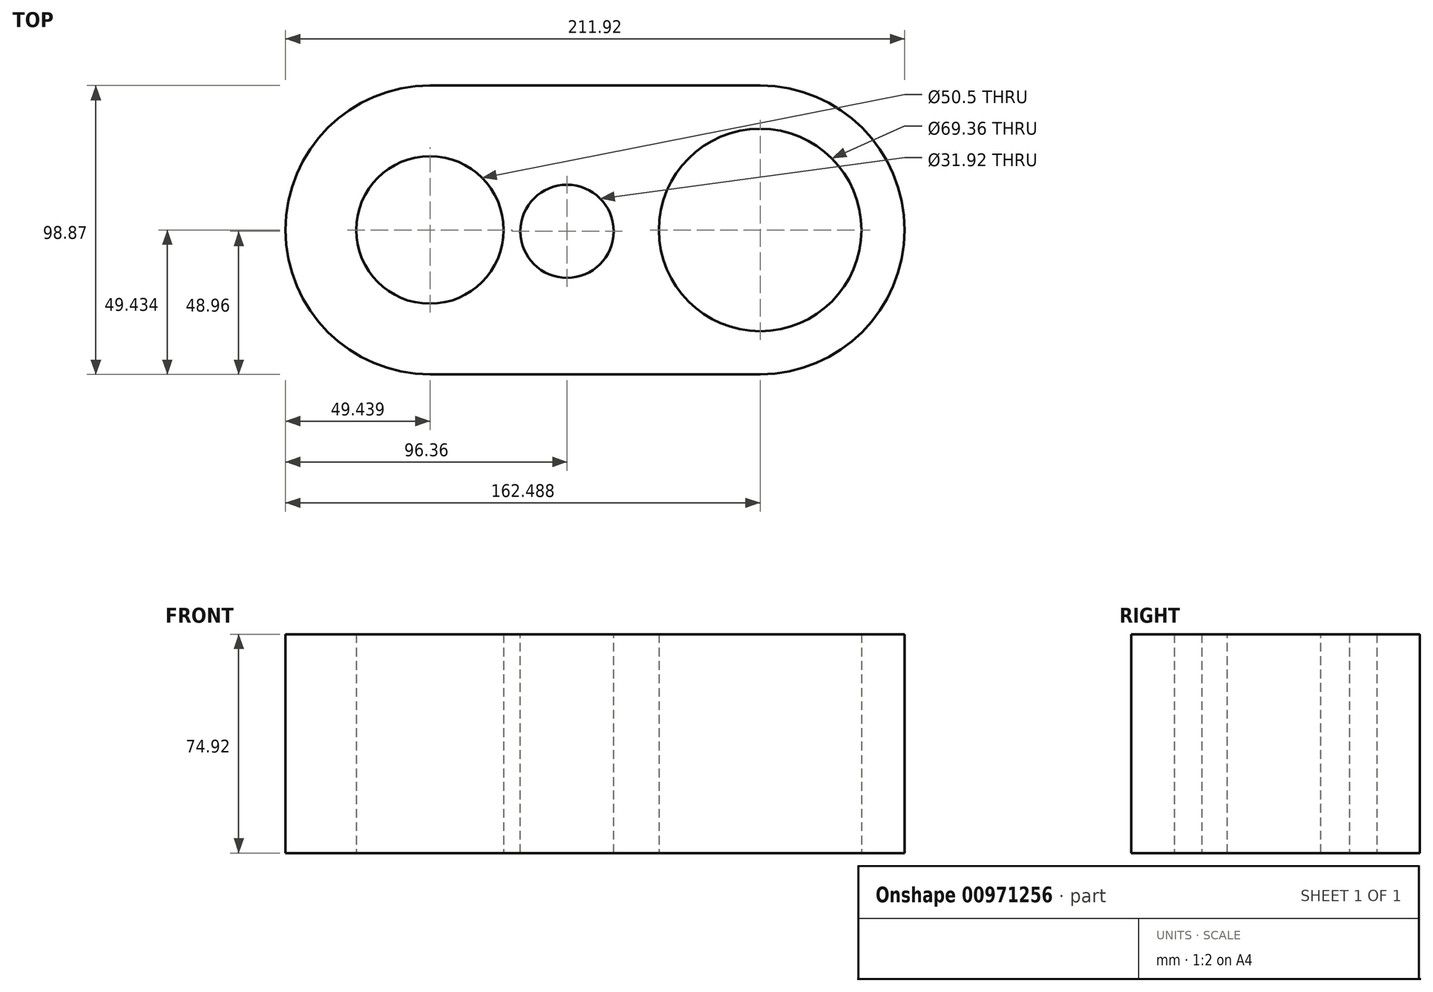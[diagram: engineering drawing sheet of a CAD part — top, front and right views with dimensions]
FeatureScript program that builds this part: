
annotation { "Feature Type Name" : "Feature", "Feature Type Description" : "" }
export const myFeature = defineFeature(function(context is Context, id is Id, definition is map)
    precondition{}
    {
        {
            var Q0;
            Q0=qCreatedBy(makeId("Top.planeOp"),FACE);
            var sketch = newSketch(context, id + "F0", { "sketchPlane" : qUnion([Q0])});
            skLineSegment(sketch, "E0", {"start": v(-46.92, 37.12) * mm, "end": v(66.13, 37.12) * mm});
            skLineSegment(sketch, "E1", {"start": v(-46.92, -61.75) * mm, "end": v(66.13, -61.75) * mm});
            skArc(sketch, "E2", {"start": v(-46.92, 37.12) * mm, "mid": v(-96.36, -12.32) * mm, "end": v(-46.92, -61.75) * mm});
            skArc(sketch, "E3", {"start": v(66.13, -61.75) * mm, "mid": v(115.56, -12.32) * mm, "end": v(66.13, 37.12) * mm});
            skCircle(sketch, "E4", {"center": v(-46.92, -12.32) * mm, "radius": 25.25 * mm});
            skCircle(sketch, "E5", {"center": v(66.13, -12.32) * mm, "radius": 34.68 * mm});
            skSolve(sketch);
        }
        {
            var Q0;
            Q0=makeQuery(id+"F0.imprint","IMPRINT",FACE,{"disambiguationData":[TD([[makeQuery(id+"F0.imprint","IMPRINT",EDGE,{"derivedFrom":sQuery(id+"F0.wireOp",EDGE,"E0")}),-1.0]])]});
            extrude(context, id + "F1", {"entities" : qUnion([Q0]), "depth" : 74.92 * mm, "offsetDistance" : 25.4 * mm});
        }
        {
            var Q0;
            Q0=makeQuery(id+"F1.opExtrude","CAP_FACE",FACE,{"disambiguationData":[OSD([sQuery(id+"F0.wireOp",EDGE,"E0"),sQuery(id+"F0.wireOp",EDGE,"E1"),sQuery(id+"F0.wireOp",EDGE,"E2"),sQuery(id+"F0.wireOp",EDGE,"E3"),sQuery(id+"F0.wireOp",EDGE,"E4"),sQuery(id+"F0.wireOp",EDGE,"E5")])],"isStart":false});
            var sketch = newSketch(context, id + "F2", { "sketchPlane" : qUnion([Q0])});
            skLineSegment(sketch, "E6", {"start": v(-46.92, -12.32) * mm, "end": v(66.13, -12.32) * mm, "construction": true});
            skSolve(sketch);
        }
        {
            var Q0;
            Q0=makeQuery(id+"F2.imprint","IMPRINT",FACE,{"disambiguationData":[TD([[makeQuery(id+"F2.imprint","IMPRINT",EDGE,{"derivedFrom":makeQuery(id+"F1.opExtrude","CAP_EDGE",EDGE,{"disambiguationData":[OSD([sQuery(id+"F0.wireOp",EDGE,"E0")])],"isStart":false})}),-1.0]])]});
            var sketch = newSketch(context, id + "F3", { "sketchPlane" : qUnion([Q0])});
            skCircle(sketch, "E7", {"center": v(0, -12.8) * mm, "radius": 15.96 * mm});
            skSolve(sketch);
        }
        {
            var Q0;
            Q0=makeQuery(id+"F3.imprint","IMPRINT",FACE,{"disambiguationData":[TD([[makeQuery(id+"F3.imprint","IMPRINT",EDGE,{"derivedFrom":sQuery(id+"F3.wireOp",EDGE,"E7")}),1.0]])]});
            extrude(context, id + "F4", {"entities" : qUnion([Q0]), "operationType" : NewBodyOperationType.REMOVE, "oppositeDirection" : true, "depth" : 166.15 * mm, "offsetDistance" : 25.4 * mm});
        }
    });
